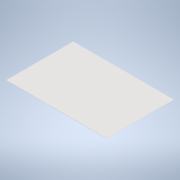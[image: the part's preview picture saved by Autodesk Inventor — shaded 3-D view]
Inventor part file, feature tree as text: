
AUTODESK INVENTOR PART (.ipt)
format: ipt  version: 2022 (Build 260153000, 153)  size: 92,160 bytes
history: native  units: mm
features: extrude x1, sketch x1
ambient origin geometry x8: Origin, YZ Plane, XZ Plane, XY Plane, X Axis, Y Axis, Z Axis, Center Point
bodies: Solid1 (feature_tree)
feature tree (2):
  extrude  "Extrusion1"  Depth=500.0mm
  sketch  "Sketch1"  dims[d0=750.0mm d1=500.0mm d2=250.0mm d3=375.0mm d4=1.0mm d5=0.0mm]
